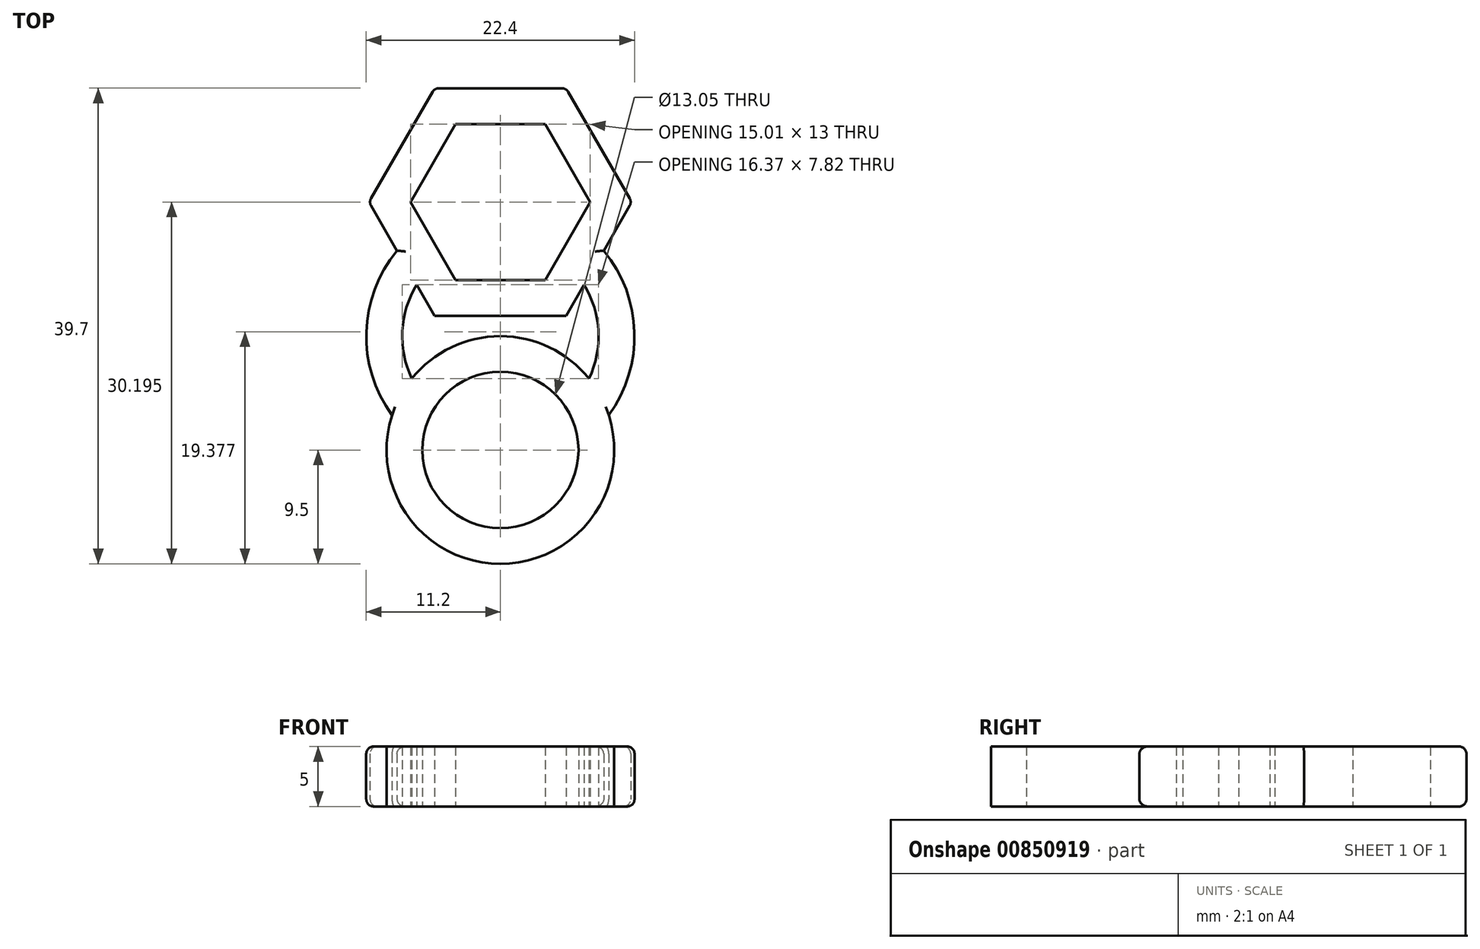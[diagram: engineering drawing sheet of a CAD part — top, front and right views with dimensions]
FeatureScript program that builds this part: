
annotation { "Feature Type Name" : "Feature", "Feature Type Description" : "" }
export const myFeature = defineFeature(function(context is Context, id is Id, definition is map)
    precondition{}
    {
        {
            var Q0;
            Q0=qCreatedBy(makeId("Top.planeOp"),FACE);
            var sketch = newSketch(context, id + "F0", { "sketchPlane" : qUnion([Q0])});
            skCircle(sketch, "E0", {"center": v(0, 0) * mm, "radius": 6.53 * mm});
            skCircle(sketch, "E1", {"center": v(0, 0) * mm, "radius": 9.5 * mm});
            skCircle(sketch, "E2.cCircle", {"center": v(0, 20.7) * mm, "radius": 6.5 * mm, "construction": true});
            skLineSegment(sketch, "E2.0", {"start": v(-3.75, 27.2) * mm, "end": v(3.75, 27.2) * mm});
            skLineSegment(sketch, "E2.1", {"start": v(3.75, 27.2) * mm, "end": v(7.5, 20.7) * mm});
            skLineSegment(sketch, "E2.2", {"start": v(7.5, 20.7) * mm, "end": v(3.75, 14.2) * mm});
            skLineSegment(sketch, "E2.3", {"start": v(3.75, 14.2) * mm, "end": v(-3.75, 14.2) * mm});
            skLineSegment(sketch, "E2.4", {"start": v(-3.75, 14.2) * mm, "end": v(-7.5, 20.7) * mm});
            skLineSegment(sketch, "E2.5", {"start": v(-7.5, 20.7) * mm, "end": v(-3.75, 27.2) * mm});
            skPoint(sketch, "E2.0.midPoint", {"position": v(0, 27.2) * mm});
            skCircle(sketch, "E3.cCircle", {"center": v(0, 20.7) * mm, "radius": 9.5 * mm, "construction": true});
            skLineSegment(sketch, "E3.0", {"start": v(5.48, 11.2) * mm, "end": v(-5.48, 11.2) * mm});
            skLineSegment(sketch, "E3.1", {"start": v(-5.48, 11.2) * mm, "end": v(-10.97, 20.7) * mm});
            skLineSegment(sketch, "E3.2", {"start": v(-10.97, 20.7) * mm, "end": v(-5.48, 30.2) * mm});
            skLineSegment(sketch, "E3.3", {"start": v(-5.48, 30.2) * mm, "end": v(5.48, 30.2) * mm});
            skLineSegment(sketch, "E3.4", {"start": v(5.48, 30.2) * mm, "end": v(10.97, 20.7) * mm});
            skLineSegment(sketch, "E3.5", {"start": v(10.97, 20.7) * mm, "end": v(5.48, 11.2) * mm});
            skPoint(sketch, "E3.0.midPoint", {"position": v(0, 11.2) * mm});
            skCircle(sketch, "E4", {"center": v(0, 9.5) * mm, "radius": 11.2 * mm});
            skCircle(sketch, "E5", {"center": v(0, 9.5) * mm, "radius": 8.2 * mm});
            skSolve(sketch);
        }
        {
            var Q0;
            Q0=makeQuery(id+"F0.imprint","IMPRINT",FACE,{"disambiguationData":[TD([[makeQuery(id+"F0.imprint","IMPRINT",EDGE,{"derivedFrom":sQuery(id+"F0.wireOp",EDGE,"E2.0")}),1.0]])]});
            var Q1;
            {var subQ1=sQuery(id+"F0.wireOp",EDGE,"E2.3");Q1=makeQuery(id+"F0.imprint","IMPRINT",FACE,{"disambiguationData":[TD([[makeQuery(id+"F0.imprint","IMPRINT",EDGE,{"derivedFrom":subQ1}),1.0]])]});}
            var Q2;
            {var subQ0=sQuery(id+"F0.wireOp",EDGE,"E4");var subQ1=sQuery(id+"F0.wireOp",EDGE,"E2.2");var subQ2=makeQuery(id+"F0.imprint","INTERSECT",VERTEX,{"derivedFrom":[subQ1,subQ0]});Q2=makeQuery(id+"F0.imprint","IMPRINT",FACE,{"disambiguationData":[TD([[makeQuery(id+"F0.imprint","IMPRINT",EDGE,{"disambiguationData":[TD([[subQ2,-1.0]])],"derivedFrom":subQ1}),1.0]])]});}
            var Q3;
            {var subQ0=sQuery(id+"F0.wireOp",EDGE,"E5");var subQ1=sQuery(id+"F0.wireOp",EDGE,"E2.4");var subQ2=makeQuery(id+"F0.imprint","INTERSECT",VERTEX,{"derivedFrom":[subQ1,subQ0]});Q3=makeQuery(id+"F0.imprint","IMPRINT",FACE,{"disambiguationData":[TD([[makeQuery(id+"F0.imprint","IMPRINT",EDGE,{"disambiguationData":[TD([[subQ2,-1.0]])],"derivedFrom":subQ1}),1.0]])]});}
            var Q4;
            {var subQ0=sQuery(id+"F0.wireOp",EDGE,"E4");var subQ1=sQuery(id+"F0.wireOp",EDGE,"E1");var subQ2=makeQuery(id+"F0.imprint","INTERSECT",VERTEX,{"disambiguationData":[OD(1.0)],"derivedFrom":[subQ1,subQ0]});Q4=makeQuery(id+"F0.imprint","IMPRINT",FACE,{"disambiguationData":[TD([[makeQuery(id+"F0.imprint","IMPRINT",EDGE,{"disambiguationData":[TD([[subQ2,1.0]])],"derivedFrom":subQ1}),-1.0]])]});}
            var Q5;
            {var subQ0=sQuery(id+"F0.wireOp",EDGE,"E4");var subQ1=sQuery(id+"F0.wireOp",EDGE,"E1");var subQ2=makeQuery(id+"F0.imprint","INTERSECT",VERTEX,{"disambiguationData":[OD(0.0)],"derivedFrom":[subQ1,subQ0]});Q5=makeQuery(id+"F0.imprint","IMPRINT",FACE,{"disambiguationData":[TD([[makeQuery(id+"F0.imprint","IMPRINT",EDGE,{"disambiguationData":[TD([[subQ2,-1.0]])],"derivedFrom":subQ1}),-1.0]])]});}
            var Q6;
            {var subQ0=sQuery(id+"F0.wireOp",EDGE,"E4");var subQ1=sQuery(id+"F0.wireOp",EDGE,"E0");var subQ2=makeQuery(id+"F0.imprint","INTERSECT",VERTEX,{"disambiguationData":[OD(0.0)],"derivedFrom":[subQ1,subQ0]});Q6=makeQuery(id+"F0.imprint","IMPRINT",FACE,{"disambiguationData":[TD([[makeQuery(id+"F0.imprint","IMPRINT",EDGE,{"disambiguationData":[TD([[subQ2,1.0]])],"derivedFrom":subQ1}),-1.0]])]});}
            var Q7;
            {var subQ0=sQuery(id+"F0.wireOp",EDGE,"E5");var subQ1=sQuery(id+"F0.wireOp",EDGE,"E0");var subQ2=makeQuery(id+"F0.imprint","INTERSECT",VERTEX,{"disambiguationData":[OD(0.0)],"derivedFrom":[subQ1,subQ0]});Q7=makeQuery(id+"F0.imprint","IMPRINT",FACE,{"disambiguationData":[TD([[makeQuery(id+"F0.imprint","IMPRINT",EDGE,{"disambiguationData":[TD([[subQ2,1.0]])],"derivedFrom":subQ1}),-1.0]])]});}
            var Q8;
            {var subQ0=sQuery(id+"F0.wireOp",EDGE,"E5");var subQ1=sQuery(id+"F0.wireOp",EDGE,"E0");var subQ2=makeQuery(id+"F0.imprint","INTERSECT",VERTEX,{"disambiguationData":[OD(0.0)],"derivedFrom":[subQ1,subQ0]});Q8=makeQuery(id+"F0.imprint","IMPRINT",FACE,{"disambiguationData":[TD([[makeQuery(id+"F0.imprint","IMPRINT",EDGE,{"disambiguationData":[TD([[subQ2,-1.0]])],"derivedFrom":subQ1}),-1.0]])]});}
            var Q9;
            {var subQ0=sQuery(id+"F0.wireOp",EDGE,"E5");var subQ1=sQuery(id+"F0.wireOp",EDGE,"E0");var subQ2=makeQuery(id+"F0.imprint","INTERSECT",VERTEX,{"disambiguationData":[OD(1.0)],"derivedFrom":[subQ1,subQ0]});Q9=makeQuery(id+"F0.imprint","IMPRINT",FACE,{"disambiguationData":[TD([[makeQuery(id+"F0.imprint","IMPRINT",EDGE,{"disambiguationData":[TD([[subQ2,-1.0]])],"derivedFrom":subQ1}),-1.0]])]});}
            extrude(context, id + "F1", {"entities" : qUnion([Q0, Q1, Q2, Q3, Q4, Q5, Q6, Q7, Q8, Q9]), "depth" : 5 * mm, "offsetDistance" : 25 * mm});
        }
        {
            var Q0;
            {var subQ0=sQuery(id+"F0.wireOp",EDGE,"E4");Q0=makeQuery(id+"F1.opExtrude","CAP_EDGE",EDGE,{"disambiguationData":[OSD([subQ0]),TDD([makeQuery(id+"F0.imprint","IMPRINT",EDGE,{"disambiguationData":[TD([[makeQuery(id+"F0.imprint","INTERSECT",VERTEX,{"disambiguationData":[OD(0.0)],"derivedFrom":[sQuery(id+"F0.wireOp",EDGE,"E1"),subQ0]}),-1.0]])],"derivedFrom":subQ0})])],"isStart":false});}
            var Q1;
            {var subQ0=sQuery(id+"F0.wireOp",EDGE,"E4");Q1=makeQuery(id+"F1.opExtrude","CAP_EDGE",EDGE,{"disambiguationData":[OSD([subQ0]),TDD([makeQuery(id+"F0.imprint","IMPRINT",EDGE,{"disambiguationData":[TD([[makeQuery(id+"F0.imprint","INTERSECT",VERTEX,{"disambiguationData":[OD(0.0)],"derivedFrom":[sQuery(id+"F0.wireOp",EDGE,"E1"),subQ0]}),-1.0]])],"derivedFrom":subQ0})])],"isStart":true});}
            var Q2;
            {var subQ0=sQuery(id+"F0.wireOp",EDGE,"E3.5");Q2=makeQuery(id+"F1.opExtrude","CAP_EDGE",EDGE,{"disambiguationData":[OSD([subQ0]),TDD([makeQuery(id+"F0.imprint","IMPRINT",EDGE,{"disambiguationData":[TD([[makeQuery(id+"F0.imprint","INTERSECT",VERTEX,{"derivedFrom":[sQuery(id+"F0.wireOp",EDGE,"E3.4"),subQ0]}),-1.0]])],"derivedFrom":subQ0})])],"isStart":true});}
            var Q3;
            {var subQ0=sQuery(id+"F0.wireOp",EDGE,"E3.5");Q3=makeQuery(id+"F1.opExtrude","CAP_EDGE",EDGE,{"disambiguationData":[OSD([subQ0]),TDD([makeQuery(id+"F0.imprint","IMPRINT",EDGE,{"disambiguationData":[TD([[makeQuery(id+"F0.imprint","INTERSECT",VERTEX,{"derivedFrom":[sQuery(id+"F0.wireOp",EDGE,"E3.4"),subQ0]}),-1.0]])],"derivedFrom":subQ0})])],"isStart":false});}
            var Q4;
            Q4=makeQuery(id+"F1.opExtrude","CAP_EDGE",EDGE,{"disambiguationData":[OSD([sQuery(id+"F0.wireOp",EDGE,"E3.4")])],"isStart":false});
            var Q5;
            Q5=makeQuery(id+"F1.opExtrude","CAP_EDGE",EDGE,{"disambiguationData":[OSD([sQuery(id+"F0.wireOp",EDGE,"E3.3")])],"isStart":false});
            var Q6;
            Q6=makeQuery(id+"F1.opExtrude","CAP_EDGE",EDGE,{"disambiguationData":[OSD([sQuery(id+"F0.wireOp",EDGE,"E3.3")])],"isStart":true});
            var Q7;
            Q7=makeQuery(id+"F1.opExtrude","CAP_EDGE",EDGE,{"disambiguationData":[OSD([sQuery(id+"F0.wireOp",EDGE,"E3.4")])],"isStart":true});
            var Q8;
            Q8=makeQuery(id+"F1.opExtrude","CAP_EDGE",EDGE,{"disambiguationData":[OSD([sQuery(id+"F0.wireOp",EDGE,"E3.2")])],"isStart":true});
            var Q9;
            Q9=makeQuery(id+"F1.opExtrude","CAP_EDGE",EDGE,{"disambiguationData":[OSD([sQuery(id+"F0.wireOp",EDGE,"E3.2")])],"isStart":false});
            var Q10;
            {var subQ0=sQuery(id+"F0.wireOp",EDGE,"E4");Q10=makeQuery(id+"F1.opExtrude","CAP_EDGE",EDGE,{"disambiguationData":[OSD([subQ0]),TDD([makeQuery(id+"F0.imprint","IMPRINT",EDGE,{"disambiguationData":[TD([[makeQuery(id+"F0.imprint","INTERSECT",VERTEX,{"disambiguationData":[OD(1.0)],"derivedFrom":[sQuery(id+"F0.wireOp",EDGE,"E1"),subQ0]}),1.0]])],"derivedFrom":subQ0})])],"isStart":false});}
            var Q11;
            {var subQ0=sQuery(id+"F0.wireOp",EDGE,"E4");Q11=makeQuery(id+"F1.opExtrude","CAP_EDGE",EDGE,{"disambiguationData":[OSD([subQ0]),TDD([makeQuery(id+"F0.imprint","IMPRINT",EDGE,{"disambiguationData":[TD([[makeQuery(id+"F0.imprint","INTERSECT",VERTEX,{"disambiguationData":[OD(1.0)],"derivedFrom":[sQuery(id+"F0.wireOp",EDGE,"E1"),subQ0]}),1.0]])],"derivedFrom":subQ0})])],"isStart":true});}
            var Q12;
            {var subQ0=sQuery(id+"F0.wireOp",EDGE,"E4");Q12=makeQuery(id+"FayhXRr06MC0eNP_1.1.F1.opExtrude","CAP_EDGE",EDGE,{"disambiguationData":[OSD([subQ0]),TDD([makeQuery(id+"F0.imprint","IMPRINT",EDGE,{"disambiguationData":[TD([[makeQuery(id+"F0.imprint","INTERSECT",VERTEX,{"disambiguationData":[OD(0.0)],"derivedFrom":[sQuery(id+"F0.wireOp",EDGE,"E1"),subQ0]}),-1.0]])],"derivedFrom":subQ0})])],"isStart":false});}
            var Q13;
            {var subQ0=sQuery(id+"F0.wireOp",EDGE,"E4");Q13=makeQuery(id+"FayhXRr06MC0eNP_1.1.F1.opExtrude","CAP_EDGE",EDGE,{"disambiguationData":[OSD([subQ0]),TDD([makeQuery(id+"F0.imprint","IMPRINT",EDGE,{"disambiguationData":[TD([[makeQuery(id+"F0.imprint","INTERSECT",VERTEX,{"disambiguationData":[OD(0.0)],"derivedFrom":[sQuery(id+"F0.wireOp",EDGE,"E1"),subQ0]}),-1.0]])],"derivedFrom":subQ0})])],"isStart":true});}
            var Q14;
            Q14=makeQuery(id+"FayhXRr06MC0eNP_1.1.F1.opExtrude","CAP_EDGE",EDGE,{"disambiguationData":[OSD([sQuery(id+"F0.wireOp",EDGE,"E3.4")])],"isStart":true});
            var Q15;
            Q15=makeQuery(id+"FayhXRr06MC0eNP_1.1.F1.opExtrude","CAP_EDGE",EDGE,{"disambiguationData":[OSD([sQuery(id+"F0.wireOp",EDGE,"E3.3")])],"isStart":true});
            var Q16;
            {var subQ0=sQuery(id+"F0.wireOp",EDGE,"E4");Q16=makeQuery(id+"FayhXRr06MC0eNP_1.2.F1.opExtrude","CAP_EDGE",EDGE,{"disambiguationData":[OSD([subQ0]),TDD([makeQuery(id+"F0.imprint","IMPRINT",EDGE,{"disambiguationData":[TD([[makeQuery(id+"F0.imprint","INTERSECT",VERTEX,{"disambiguationData":[OD(1.0)],"derivedFrom":[sQuery(id+"F0.wireOp",EDGE,"E1"),subQ0]}),1.0]])],"derivedFrom":subQ0})])],"isStart":true});}
            var Q17;
            {var subQ0=sQuery(id+"F0.wireOp",EDGE,"E3.1");Q17=makeQuery(id+"FayhXRr06MC0eNP_1.2.F1.opExtrude","CAP_EDGE",EDGE,{"disambiguationData":[OSD([subQ0]),TDD([makeQuery(id+"F0.imprint","IMPRINT",EDGE,{"disambiguationData":[TD([[makeQuery(id+"F0.imprint","INTERSECT",VERTEX,{"derivedFrom":[subQ0,sQuery(id+"F0.wireOp",EDGE,"E3.2")]}),1.0]])],"derivedFrom":subQ0})])],"isStart":true});}
            var Q18;
            Q18=makeQuery(id+"FayhXRr06MC0eNP_1.2.F1.opExtrude","CAP_EDGE",EDGE,{"disambiguationData":[OSD([sQuery(id+"F0.wireOp",EDGE,"E3.2")])],"isStart":true});
            var Q19;
            Q19=makeQuery(id+"FayhXRr06MC0eNP_1.2.F1.opExtrude","CAP_EDGE",EDGE,{"disambiguationData":[OSD([sQuery(id+"F0.wireOp",EDGE,"E3.3")])],"isStart":true});
            var Q20;
            Q20=makeQuery(id+"FayhXRr06MC0eNP_1.2.F1.opExtrude","CAP_EDGE",EDGE,{"disambiguationData":[OSD([sQuery(id+"F0.wireOp",EDGE,"E3.4")])],"isStart":true});
            var Q21;
            {var subQ0=sQuery(id+"F0.wireOp",EDGE,"E3.5");Q21=makeQuery(id+"FayhXRr06MC0eNP_1.2.F1.opExtrude","CAP_EDGE",EDGE,{"disambiguationData":[OSD([subQ0]),TDD([makeQuery(id+"F0.imprint","IMPRINT",EDGE,{"disambiguationData":[TD([[makeQuery(id+"F0.imprint","INTERSECT",VERTEX,{"derivedFrom":[sQuery(id+"F0.wireOp",EDGE,"E3.4"),subQ0]}),-1.0]])],"derivedFrom":subQ0})])],"isStart":true});}
            var Q22;
            {var subQ0=sQuery(id+"F0.wireOp",EDGE,"E4");Q22=makeQuery(id+"FayhXRr06MC0eNP_1.2.F1.opExtrude","CAP_EDGE",EDGE,{"disambiguationData":[OSD([subQ0]),TDD([makeQuery(id+"F0.imprint","IMPRINT",EDGE,{"disambiguationData":[TD([[makeQuery(id+"F0.imprint","INTERSECT",VERTEX,{"disambiguationData":[OD(0.0)],"derivedFrom":[sQuery(id+"F0.wireOp",EDGE,"E1"),subQ0]}),-1.0]])],"derivedFrom":subQ0})])],"isStart":true});}
            var Q23;
            {var subQ0=sQuery(id+"F0.wireOp",EDGE,"E4");Q23=makeQuery(id+"FayhXRr06MC0eNP_1.1.F1.opExtrude","CAP_EDGE",EDGE,{"disambiguationData":[OSD([subQ0]),TDD([makeQuery(id+"F0.imprint","IMPRINT",EDGE,{"disambiguationData":[TD([[makeQuery(id+"F0.imprint","INTERSECT",VERTEX,{"disambiguationData":[OD(1.0)],"derivedFrom":[sQuery(id+"F0.wireOp",EDGE,"E1"),subQ0]}),1.0]])],"derivedFrom":subQ0})])],"isStart":true});}
            var Q24;
            Q24=makeQuery(id+"FayhXRr06MC0eNP_1.1.F1.opExtrude","CAP_EDGE",EDGE,{"disambiguationData":[OSD([sQuery(id+"F0.wireOp",EDGE,"E3.2")])],"isStart":true});
            var Q25;
            {var subQ0=sQuery(id+"F0.wireOp",EDGE,"E3.1");Q25=makeQuery(id+"FayhXRr06MC0eNP_1.1.F1.opExtrude","CAP_EDGE",EDGE,{"disambiguationData":[OSD([subQ0]),TDD([makeQuery(id+"F0.imprint","IMPRINT",EDGE,{"disambiguationData":[TD([[makeQuery(id+"F0.imprint","INTERSECT",VERTEX,{"derivedFrom":[subQ0,sQuery(id+"F0.wireOp",EDGE,"E3.2")]}),1.0]])],"derivedFrom":subQ0})])],"isStart":true});}
            var Q26;
            {var subQ0=sQuery(id+"F0.wireOp",EDGE,"E3.1");Q26=makeQuery(id+"F1.opExtrude","CAP_EDGE",EDGE,{"disambiguationData":[OSD([subQ0]),TDD([makeQuery(id+"F0.imprint","IMPRINT",EDGE,{"disambiguationData":[TD([[makeQuery(id+"F0.imprint","INTERSECT",VERTEX,{"derivedFrom":[subQ0,sQuery(id+"F0.wireOp",EDGE,"E3.2")]}),1.0]])],"derivedFrom":subQ0})])],"isStart":false});}
            var Q27;
            {var subQ0=sQuery(id+"F0.wireOp",EDGE,"E4");Q27=makeQuery(id+"FayhXRr06MC0eNP_1.1.F1.opExtrude","CAP_EDGE",EDGE,{"disambiguationData":[OSD([subQ0]),TDD([makeQuery(id+"F0.imprint","IMPRINT",EDGE,{"disambiguationData":[TD([[makeQuery(id+"F0.imprint","INTERSECT",VERTEX,{"disambiguationData":[OD(1.0)],"derivedFrom":[sQuery(id+"F0.wireOp",EDGE,"E1"),subQ0]}),1.0]])],"derivedFrom":subQ0})])],"isStart":false});}
            var Q28;
            {var subQ0=sQuery(id+"F0.wireOp",EDGE,"E3.1");Q28=makeQuery(id+"FayhXRr06MC0eNP_1.1.F1.opExtrude","CAP_EDGE",EDGE,{"disambiguationData":[OSD([subQ0]),TDD([makeQuery(id+"F0.imprint","IMPRINT",EDGE,{"disambiguationData":[TD([[makeQuery(id+"F0.imprint","INTERSECT",VERTEX,{"derivedFrom":[subQ0,sQuery(id+"F0.wireOp",EDGE,"E3.2")]}),1.0]])],"derivedFrom":subQ0})])],"isStart":false});}
            var Q29;
            Q29=makeQuery(id+"FayhXRr06MC0eNP_1.1.F1.opExtrude","CAP_EDGE",EDGE,{"disambiguationData":[OSD([sQuery(id+"F0.wireOp",EDGE,"E3.2")])],"isStart":false});
            var Q30;
            Q30=makeQuery(id+"FayhXRr06MC0eNP_1.1.F1.opExtrude","CAP_EDGE",EDGE,{"disambiguationData":[OSD([sQuery(id+"F0.wireOp",EDGE,"E3.3")])],"isStart":false});
            var Q31;
            Q31=makeQuery(id+"FayhXRr06MC0eNP_1.1.F1.opExtrude","CAP_EDGE",EDGE,{"disambiguationData":[OSD([sQuery(id+"F0.wireOp",EDGE,"E3.4")])],"isStart":false});
            var Q32;
            {var subQ0=sQuery(id+"F0.wireOp",EDGE,"E3.5");Q32=makeQuery(id+"FayhXRr06MC0eNP_1.1.F1.opExtrude","CAP_EDGE",EDGE,{"disambiguationData":[OSD([subQ0]),TDD([makeQuery(id+"F0.imprint","IMPRINT",EDGE,{"disambiguationData":[TD([[makeQuery(id+"F0.imprint","INTERSECT",VERTEX,{"derivedFrom":[sQuery(id+"F0.wireOp",EDGE,"E3.4"),subQ0]}),-1.0]])],"derivedFrom":subQ0})])],"isStart":false});}
            var Q33;
            {var subQ0=sQuery(id+"F0.wireOp",EDGE,"E3.5");Q33=makeQuery(id+"FayhXRr06MC0eNP_1.1.F1.opExtrude","CAP_EDGE",EDGE,{"disambiguationData":[OSD([subQ0]),TDD([makeQuery(id+"F0.imprint","IMPRINT",EDGE,{"disambiguationData":[TD([[makeQuery(id+"F0.imprint","INTERSECT",VERTEX,{"derivedFrom":[sQuery(id+"F0.wireOp",EDGE,"E3.4"),subQ0]}),-1.0]])],"derivedFrom":subQ0})])],"isStart":true});}
            var Q34;
            {var subQ0=sQuery(id+"F0.wireOp",EDGE,"E3.1");Q34=makeQuery(id+"F1.opExtrude","CAP_EDGE",EDGE,{"disambiguationData":[OSD([subQ0]),TDD([makeQuery(id+"F0.imprint","IMPRINT",EDGE,{"disambiguationData":[TD([[makeQuery(id+"F0.imprint","INTERSECT",VERTEX,{"derivedFrom":[subQ0,sQuery(id+"F0.wireOp",EDGE,"E3.2")]}),1.0]])],"derivedFrom":subQ0})])],"isStart":true});}
            var Q35;
            Q35=makeQuery(id+"FayhXRr06MC0eNP_1.1.F1.opExtrude","SWEPT_EDGE",EDGE,{"disambiguationData":[OSD([sQuery(id+"F0.wireOp",EDGE,"E3.3"),sQuery(id+"F0.wireOp",EDGE,"E3.4")])]});
            var Q36;
            Q36=makeQuery(id+"FayhXRr06MC0eNP_1.1.F1.opExtrude","SWEPT_EDGE",EDGE,{"disambiguationData":[OSD([sQuery(id+"F0.wireOp",EDGE,"E3.2"),sQuery(id+"F0.wireOp",EDGE,"E3.3")])]});
            var Q37;
            Q37=makeQuery(id+"FayhXRr06MC0eNP_1.1.F1.opExtrude","SWEPT_EDGE",EDGE,{"disambiguationData":[OSD([sQuery(id+"F0.wireOp",EDGE,"E3.1"),sQuery(id+"F0.wireOp",EDGE,"E3.2")])]});
            var Q38;
            Q38=makeQuery(id+"FayhXRr06MC0eNP_1.1.F1.opExtrude","SWEPT_EDGE",EDGE,{"disambiguationData":[OSD([sQuery(id+"F0.wireOp",EDGE,"E3.4"),sQuery(id+"F0.wireOp",EDGE,"E3.5")])]});
            var Q39;
            Q39=makeQuery(id+"F1.opExtrude","SWEPT_EDGE",EDGE,{"disambiguationData":[OSD([sQuery(id+"F0.wireOp",EDGE,"E3.1"),sQuery(id+"F0.wireOp",EDGE,"E3.2")])]});
            var Q40;
            Q40=makeQuery(id+"F1.opExtrude","SWEPT_EDGE",EDGE,{"disambiguationData":[OSD([sQuery(id+"F0.wireOp",EDGE,"E3.2"),sQuery(id+"F0.wireOp",EDGE,"E3.3")])]});
            var Q41;
            Q41=makeQuery(id+"F1.opExtrude","SWEPT_EDGE",EDGE,{"disambiguationData":[OSD([sQuery(id+"F0.wireOp",EDGE,"E3.3"),sQuery(id+"F0.wireOp",EDGE,"E3.4")])]});
            var Q42;
            Q42=makeQuery(id+"F1.opExtrude","SWEPT_EDGE",EDGE,{"disambiguationData":[OSD([sQuery(id+"F0.wireOp",EDGE,"E3.4"),sQuery(id+"F0.wireOp",EDGE,"E3.5")])]});
            var Q43;
            Q43=makeQuery(id+"FayhXRr06MC0eNP_1.2.F1.opExtrude","SWEPT_EDGE",EDGE,{"disambiguationData":[OSD([sQuery(id+"F0.wireOp",EDGE,"E3.1"),sQuery(id+"F0.wireOp",EDGE,"E3.2")])]});
            var Q44;
            Q44=makeQuery(id+"FayhXRr06MC0eNP_1.2.F1.opExtrude","SWEPT_EDGE",EDGE,{"disambiguationData":[OSD([sQuery(id+"F0.wireOp",EDGE,"E3.2"),sQuery(id+"F0.wireOp",EDGE,"E3.3")])]});
            var Q45;
            Q45=makeQuery(id+"FayhXRr06MC0eNP_1.2.F1.opExtrude","SWEPT_EDGE",EDGE,{"disambiguationData":[OSD([sQuery(id+"F0.wireOp",EDGE,"E3.3"),sQuery(id+"F0.wireOp",EDGE,"E3.4")])]});
            var Q46;
            Q46=makeQuery(id+"FayhXRr06MC0eNP_1.2.F1.opExtrude","SWEPT_EDGE",EDGE,{"disambiguationData":[OSD([sQuery(id+"F0.wireOp",EDGE,"E3.4"),sQuery(id+"F0.wireOp",EDGE,"E3.5")])]});
            var Q47;
            Q47=makeQuery(id+"FayhXRr06MC0eNP_1.2.F1.opExtrude","CAP_EDGE",EDGE,{"disambiguationData":[OSD([sQuery(id+"F0.wireOp",EDGE,"E3.2")])],"isStart":false});
            var Q48;
            {var subQ0=sQuery(id+"F0.wireOp",EDGE,"E3.1");Q48=makeQuery(id+"FayhXRr06MC0eNP_1.2.F1.opExtrude","CAP_EDGE",EDGE,{"disambiguationData":[OSD([subQ0]),TDD([makeQuery(id+"F0.imprint","IMPRINT",EDGE,{"disambiguationData":[TD([[makeQuery(id+"F0.imprint","INTERSECT",VERTEX,{"derivedFrom":[subQ0,sQuery(id+"F0.wireOp",EDGE,"E3.2")]}),1.0]])],"derivedFrom":subQ0})])],"isStart":false});}
            var Q49;
            Q49=makeQuery(id+"FayhXRr06MC0eNP_1.2.F1.opExtrude","CAP_EDGE",EDGE,{"disambiguationData":[OSD([sQuery(id+"F0.wireOp",EDGE,"E3.3")])],"isStart":false});
            var Q50;
            Q50=makeQuery(id+"FayhXRr06MC0eNP_1.2.F1.opExtrude","CAP_EDGE",EDGE,{"disambiguationData":[OSD([sQuery(id+"F0.wireOp",EDGE,"E3.4")])],"isStart":false});
            var Q51;
            {var subQ0=sQuery(id+"F0.wireOp",EDGE,"E3.5");Q51=makeQuery(id+"FayhXRr06MC0eNP_1.2.F1.opExtrude","CAP_EDGE",EDGE,{"disambiguationData":[OSD([subQ0]),TDD([makeQuery(id+"F0.imprint","IMPRINT",EDGE,{"disambiguationData":[TD([[makeQuery(id+"F0.imprint","INTERSECT",VERTEX,{"derivedFrom":[sQuery(id+"F0.wireOp",EDGE,"E3.4"),subQ0]}),-1.0]])],"derivedFrom":subQ0})])],"isStart":false});}
            var Q52;
            {var subQ0=sQuery(id+"F0.wireOp",EDGE,"E4");Q52=makeQuery(id+"FayhXRr06MC0eNP_1.2.F1.opExtrude","CAP_EDGE",EDGE,{"disambiguationData":[OSD([subQ0]),TDD([makeQuery(id+"F0.imprint","IMPRINT",EDGE,{"disambiguationData":[TD([[makeQuery(id+"F0.imprint","INTERSECT",VERTEX,{"disambiguationData":[OD(0.0)],"derivedFrom":[sQuery(id+"F0.wireOp",EDGE,"E1"),subQ0]}),-1.0]])],"derivedFrom":subQ0})])],"isStart":false});}
            var Q53;
            {var subQ0=sQuery(id+"F0.wireOp",EDGE,"E4");Q53=makeQuery(id+"FayhXRr06MC0eNP_1.2.F1.opExtrude","CAP_EDGE",EDGE,{"disambiguationData":[OSD([subQ0]),TDD([makeQuery(id+"F0.imprint","IMPRINT",EDGE,{"disambiguationData":[TD([[makeQuery(id+"F0.imprint","INTERSECT",VERTEX,{"disambiguationData":[OD(1.0)],"derivedFrom":[sQuery(id+"F0.wireOp",EDGE,"E1"),subQ0]}),1.0]])],"derivedFrom":subQ0})])],"isStart":false});}
            fillet(context, id + "F2", {"entities" : qUnion([Q0, Q1, Q2, Q3, Q4, Q5, Q6, Q7, Q8, Q9, Q10, Q11, Q12, Q13, Q14, Q15, Q16, Q17, Q18, Q19, Q20, Q21, Q22, Q23, Q24, Q25, Q26, Q27, Q28, Q29, Q30, Q31, Q32, Q33, Q34, Q35, Q36, Q37, Q38, Q39, Q40, Q41, Q42, Q43, Q44, Q45, Q46, Q47, Q48, Q49, Q50, Q51, Q52, Q53]), "radius" : .6 * mm, "tangentPropagation" : true, "allowEdgeOverflow" : false});
        }
    });
